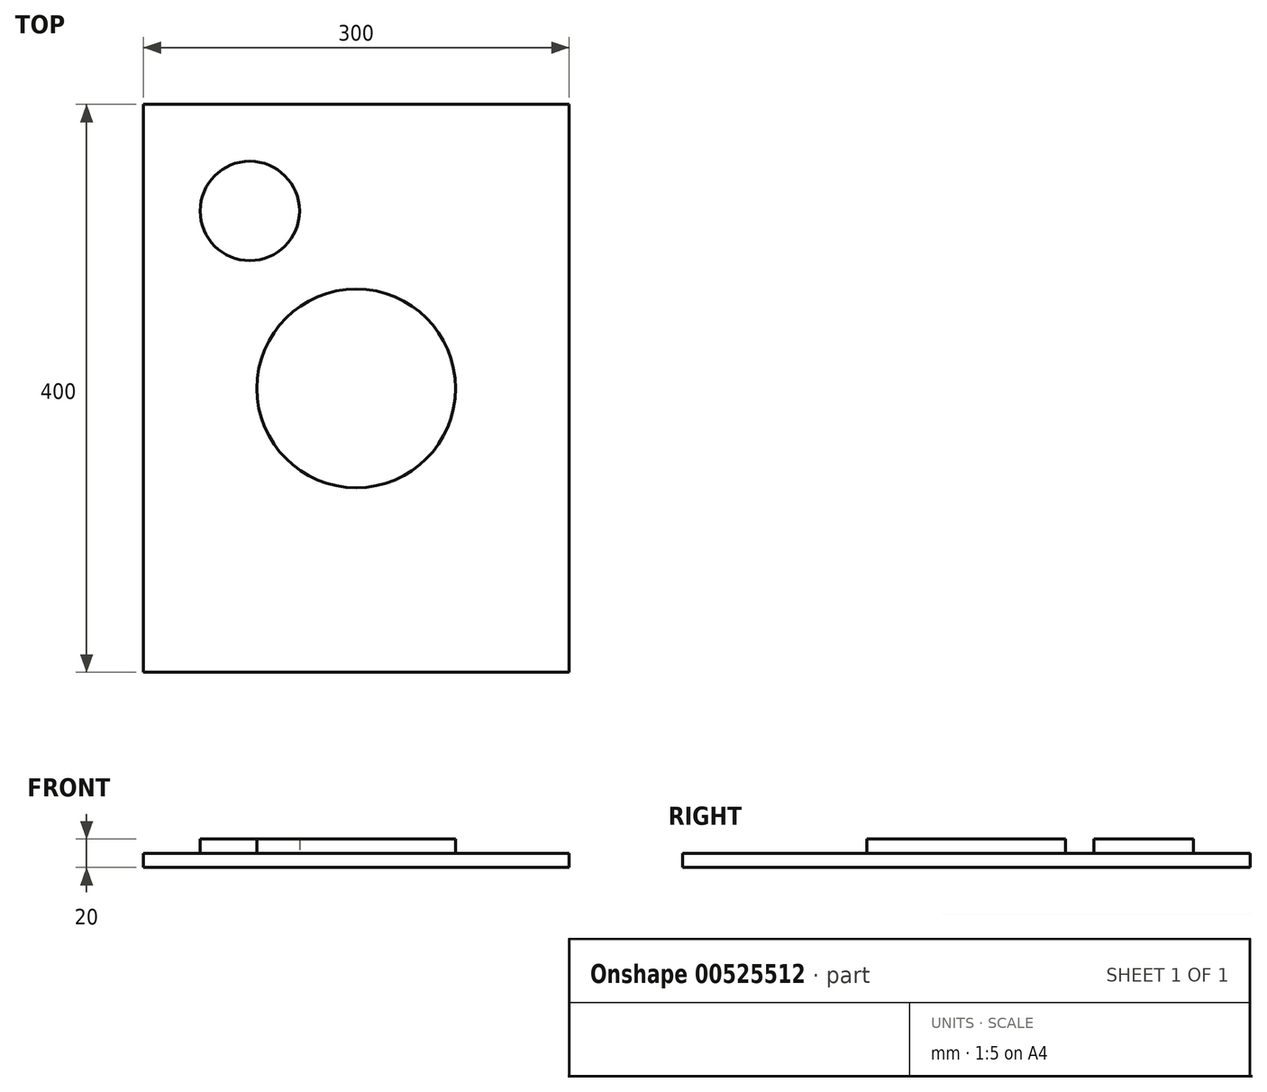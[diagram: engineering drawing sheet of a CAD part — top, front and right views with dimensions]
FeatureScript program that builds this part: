
annotation { "Feature Type Name" : "Feature", "Feature Type Description" : "" }
export const myFeature = defineFeature(function(context is Context, id is Id, definition is map)
    precondition{}
    {
        {
            var Q0;
            Q0=qCreatedBy(makeId("Top.planeOp"),FACE);
            var sketch = newSketch(context, id + "F0", { "sketchPlane" : qUnion([Q0])});
            skLineSegment(sketch, "E0.bottom", {"start": v(150, -200) * mm, "end": v(-150, -200) * mm});
            skLineSegment(sketch, "E0.top", {"start": v(150, 200) * mm, "end": v(-150, 200) * mm});
            skLineSegment(sketch, "E0.left", {"start": v(150, -200) * mm, "end": v(150, 200) * mm});
            skLineSegment(sketch, "E0.right", {"start": v(-150, -200) * mm, "end": v(-150, 200) * mm});
            skPoint(sketch, "E0.middle", {"position": v(0, 0) * mm});
            skSolve(sketch);
        }
        {
            var Q0;
            Q0=makeQuery(id+"F0.imprint","IMPRINT",FACE,{"disambiguationData":[TD([[makeQuery(id+"F0.imprint","IMPRINT",EDGE,{"derivedFrom":sQuery(id+"F0.wireOp",EDGE,"E0.bottom")}),-1.0]])]});
            extrude(context, id + "F1", {"entities" : qUnion([Q0]), "depth" : 10 * mm, "offsetDistance" : 25 * mm});
        }
        {
            var Q0;
            Q0=makeQuery(id+"F1.opExtrude","CAP_FACE",FACE,{"disambiguationData":[OSD([sQuery(id+"F0.wireOp",EDGE,"E0.bottom"),sQuery(id+"F0.wireOp",EDGE,"E0.top"),sQuery(id+"F0.wireOp",EDGE,"E0.left"),sQuery(id+"F0.wireOp",EDGE,"E0.right")])],"isStart":false});
            var sketch = newSketch(context, id + "F2", { "sketchPlane" : qUnion([Q0])});
            skCircle(sketch, "E1", {"center": v(-75, 125) * mm, "radius": 35 * mm});
            skSolve(sketch);
        }
        {
            var Q0;
            Q0=makeQuery(id+"F2.imprint","IMPRINT",FACE,{"disambiguationData":[TD([[makeQuery(id+"F2.imprint","IMPRINT",EDGE,{"derivedFrom":sQuery(id+"F2.wireOp",EDGE,"E1")}),1.0]])]});
            extrude(context, id + "F3", {"entities" : qUnion([Q0]), "operationType" : NewBodyOperationType.ADD, "depth" : 10 * mm, "offsetDistance" : 25 * mm});
        }
        {
            var Q0;
            Q0=makeQuery(id+"F1.opExtrude","CAP_FACE",FACE,{"disambiguationData":[OSD([sQuery(id+"F0.wireOp",EDGE,"E0.bottom"),sQuery(id+"F0.wireOp",EDGE,"E0.top"),sQuery(id+"F0.wireOp",EDGE,"E0.left"),sQuery(id+"F0.wireOp",EDGE,"E0.right")])],"isStart":false});
            var sketch = newSketch(context, id + "F4", { "sketchPlane" : qUnion([Q0])});
            skCircle(sketch, "E2", {"center": v(0, 0) * mm, "radius": 70 * mm});
            skSolve(sketch);
        }
        {
            var Q0;
            Q0=makeQuery(id+"F4.imprint","IMPRINT",FACE,{"disambiguationData":[TD([[makeQuery(id+"F4.imprint","IMPRINT",EDGE,{"derivedFrom":sQuery(id+"F4.wireOp",EDGE,"E2")}),1.0]])]});
            extrude(context, id + "F5", {"entities" : qUnion([Q0]), "operationType" : NewBodyOperationType.ADD, "depth" : 10 * mm, "offsetDistance" : 25 * mm});
        }
    });
